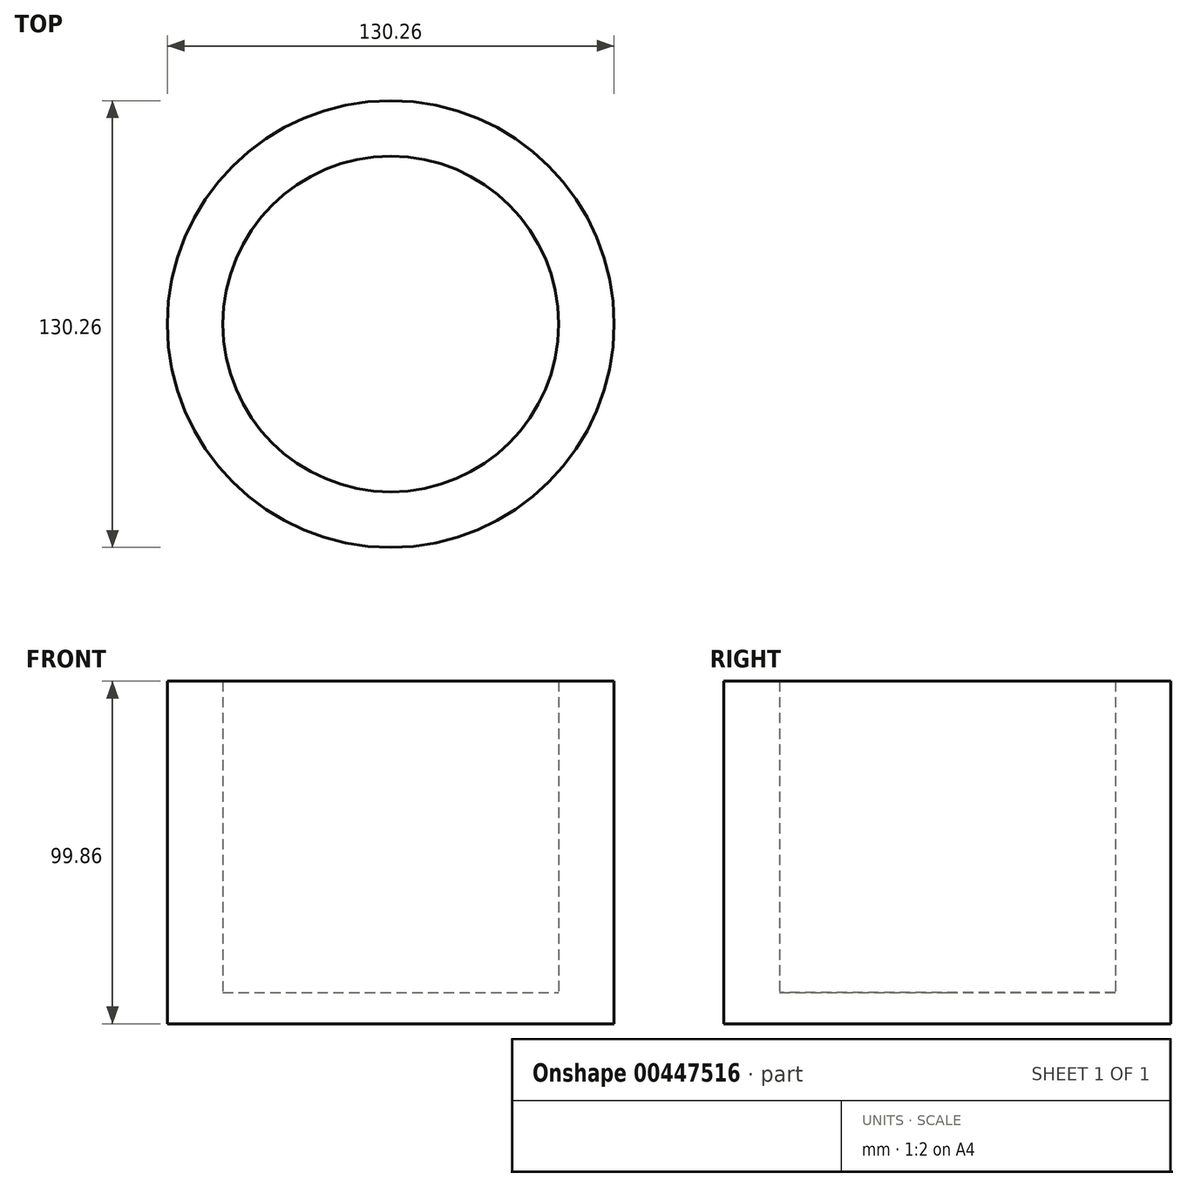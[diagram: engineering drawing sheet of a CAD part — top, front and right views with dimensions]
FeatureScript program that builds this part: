
annotation { "Feature Type Name" : "Feature", "Feature Type Description" : "" }
export const myFeature = defineFeature(function(context is Context, id is Id, definition is map)
    precondition{}
    {
        {
            var Q0;
            Q0=qCreatedBy(makeId("Front.planeOp"),FACE);
            var sketch = newSketch(context, id + "F0", { "sketchPlane" : qUnion([Q0])});
            skLineSegment(sketch, "E0", {"start": v(0, 0) * mm, "end": v(0, 86.05) * mm, "construction": true});
            skLineSegment(sketch, "E1", {"start": v(0, 0) * mm, "end": v(-26.84, 0) * mm});
            skLineSegment(sketch, "E2", {"start": v(-26.84, 0) * mm, "end": v(-48.94, 0) * mm});
            skLineSegment(sketch, "E3", {"start": v(-48.94, 0) * mm, "end": v(-48.94, 90.78) * mm});
            skLineSegment(sketch, "E4", {"start": v(-48.94, 90.78) * mm, "end": v(-65.13, 90.78) * mm});
            skLineSegment(sketch, "E5", {"start": v(-65.13, 90.78) * mm, "end": v(-65.13, -9.08) * mm});
            skLineSegment(sketch, "E6", {"start": v(-65.13, -9.08) * mm, "end": v(0, -9.08) * mm});
            skLineSegment(sketch, "E7", {"start": v(0, -9.08) * mm, "end": v(0, 0) * mm});
            skSolve(sketch);
        }
        {
            var Q0;
            Q0=makeQuery(id+"F0.imprint","IMPRINT",FACE,{"disambiguationData":[TD([[makeQuery(id+"F0.imprint","IMPRINT",EDGE,{"derivedFrom":sQuery(id+"F0.wireOp",EDGE,"E1")}),1.0]])]});
            var Q1;
            Q1=sQuery(id+"F0.wireOp",EDGE,"E0");
            revolve(context, id + "F1", {"entities" : qUnion([Q0]), "axis" : qUnion([Q1]), "revolveType" : RevolveType.FULL});
        }
    });
